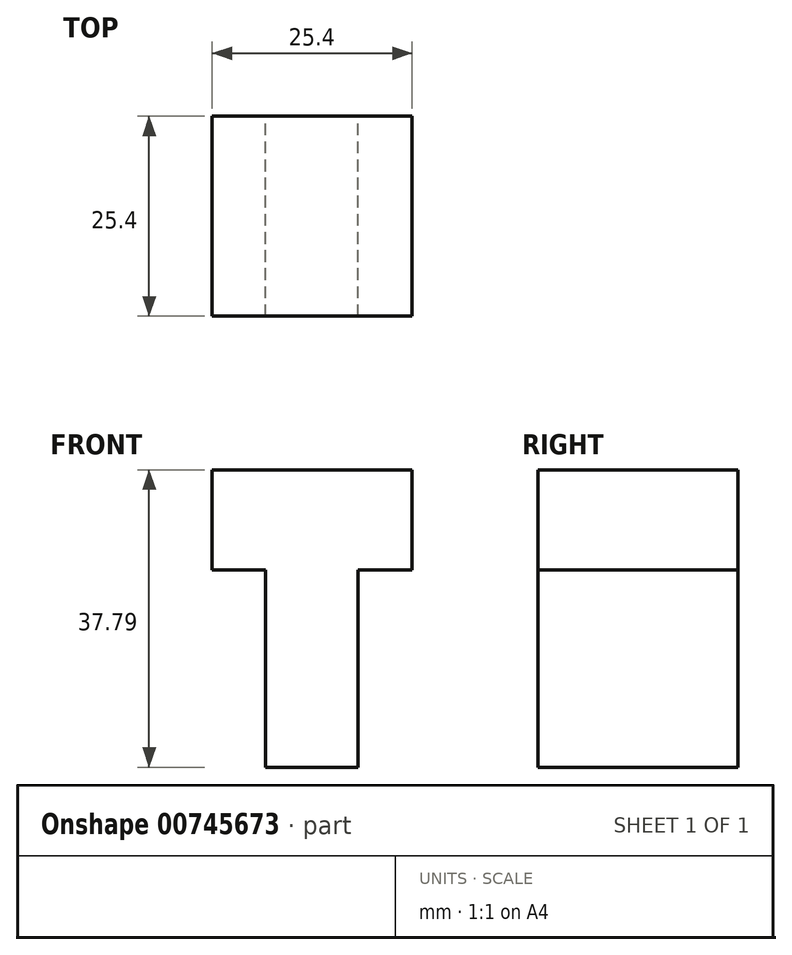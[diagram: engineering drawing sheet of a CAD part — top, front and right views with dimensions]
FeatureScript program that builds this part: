
annotation { "Feature Type Name" : "Feature", "Feature Type Description" : "" }
export const myFeature = defineFeature(function(context is Context, id is Id, definition is map)
    precondition{}
    {
        {
            var Q0;
            Q0=qCreatedBy(makeId("Front.planeOp"),FACE);
            var sketch = newSketch(context, id + "F0", { "sketchPlane" : qUnion([Q0])});
            skLineSegment(sketch, "E0", {"start": v(0, 0) * mm, "end": v(0, 25.09) * mm});
            skLineSegment(sketch, "E1", {"start": v(0, 25.09) * mm, "end": v(-6.77, 25.09) * mm});
            skLineSegment(sketch, "E2", {"start": v(-6.77, 25.09) * mm, "end": v(-6.77, 37.79) * mm});
            skLineSegment(sketch, "E3", {"start": v(-6.77, 37.79) * mm, "end": v(18.63, 37.79) * mm});
            skLineSegment(sketch, "E4", {"start": v(18.63, 37.79) * mm, "end": v(18.63, 25.09) * mm});
            skLineSegment(sketch, "E5", {"start": v(18.63, 25.09) * mm, "end": v(11.76, 25.09) * mm});
            skLineSegment(sketch, "E6", {"start": v(11.76, 25.09) * mm, "end": v(11.76, 0) * mm});
            skLineSegment(sketch, "E7", {"start": v(0, 0) * mm, "end": v(11.76, 0) * mm});
            skSolve(sketch);
        }
        {
            var Q0;
            Q0=makeQuery(id+"F0.imprint","IMPRINT",FACE,{"disambiguationData":[TD([[makeQuery(id+"F0.imprint","IMPRINT",EDGE,{"derivedFrom":sQuery(id+"F0.wireOp",EDGE,"E0")}),-1.0]])]});
            extrude(context, id + "F1", {"entities" : qUnion([Q0]), "depth" : 25.4 * mm, "offsetDistance" : 25.4 * mm});
        }
    });
